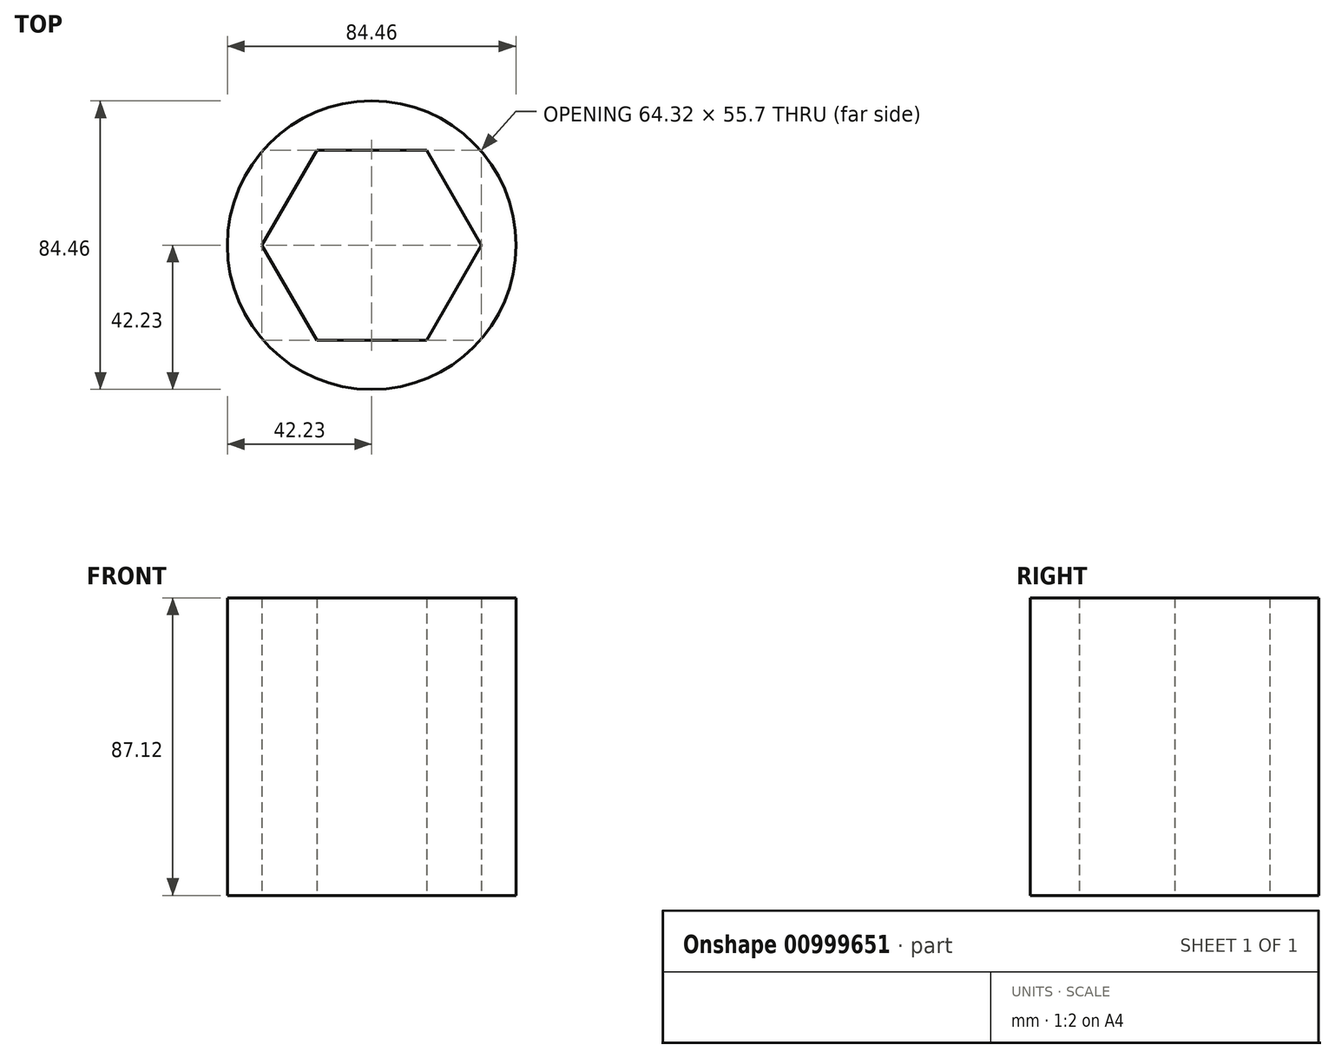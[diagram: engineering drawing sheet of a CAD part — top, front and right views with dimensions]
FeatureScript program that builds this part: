
annotation { "Feature Type Name" : "Feature", "Feature Type Description" : "" }
export const myFeature = defineFeature(function(context is Context, id is Id, definition is map)
    precondition{}
    {
        {
            var Q0;
            Q0=qCreatedBy(makeId("Top.planeOp"),FACE);
            var sketch = newSketch(context, id + "F0", { "sketchPlane" : qUnion([Q0])});
            skCircle(sketch, "E0", {"center": v(0, 0) * mm, "radius": 42.23 * mm});
            skSolve(sketch);
        }
        {
            var Q0;
            Q0=makeQuery(id+"F0.imprint","IMPRINT",FACE,{"disambiguationData":[TD([[makeQuery(id+"F0.imprint","IMPRINT",EDGE,{"derivedFrom":sQuery(id+"F0.wireOp",EDGE,"E0")}),1.0]])]});
            extrude(context, id + "F1", {"entities" : qUnion([Q0]), "oppositeDirection" : true, "depth" : 87.12 * mm, "offsetDistance" : 25.4 * mm});
        }
        {
            var Q0;
            Q0=makeQuery(id+"F1.opExtrude","CAP_FACE",FACE,{"disambiguationData":[OSD([sQuery(id+"F0.wireOp",EDGE,"E0")])],"isStart":false});
            var sketch = newSketch(context, id + "F2", { "sketchPlane" : qUnion([Q0])});
            skCircle(sketch, "E1.cCircle", {"center": v(0, 0) * mm, "radius": 27.85 * mm, "construction": true});
            skLineSegment(sketch, "E1.0", {"start": v(-16.08, 27.85) * mm, "end": v(16.08, 27.85) * mm});
            skLineSegment(sketch, "E1.1", {"start": v(16.08, 27.85) * mm, "end": v(32.16, 0) * mm});
            skLineSegment(sketch, "E1.2", {"start": v(32.16, 0) * mm, "end": v(16.08, -27.85) * mm});
            skLineSegment(sketch, "E1.3", {"start": v(16.08, -27.85) * mm, "end": v(-16.08, -27.85) * mm});
            skLineSegment(sketch, "E1.4", {"start": v(-16.08, -27.85) * mm, "end": v(-32.16, 0) * mm});
            skLineSegment(sketch, "E1.5", {"start": v(-32.16, 0) * mm, "end": v(-16.08, 27.85) * mm});
            skPoint(sketch, "E1.0.midPoint", {"position": v(0, 27.85) * mm});
            skSolve(sketch);
        }
        {
            var Q0;
            Q0=makeQuery(id+"F2.imprint","IMPRINT",FACE,{"disambiguationData":[TD([[makeQuery(id+"F2.imprint","IMPRINT",EDGE,{"derivedFrom":sQuery(id+"F2.wireOp",EDGE,"E1.0")}),-1.0]])]});
            extrude(context, id + "F3", {"entities" : qUnion([Q0]), "operationType" : NewBodyOperationType.REMOVE, "oppositeDirection" : true, "depth" : 165.86 * mm, "offsetDistance" : 25.4 * mm});
        }
    });
